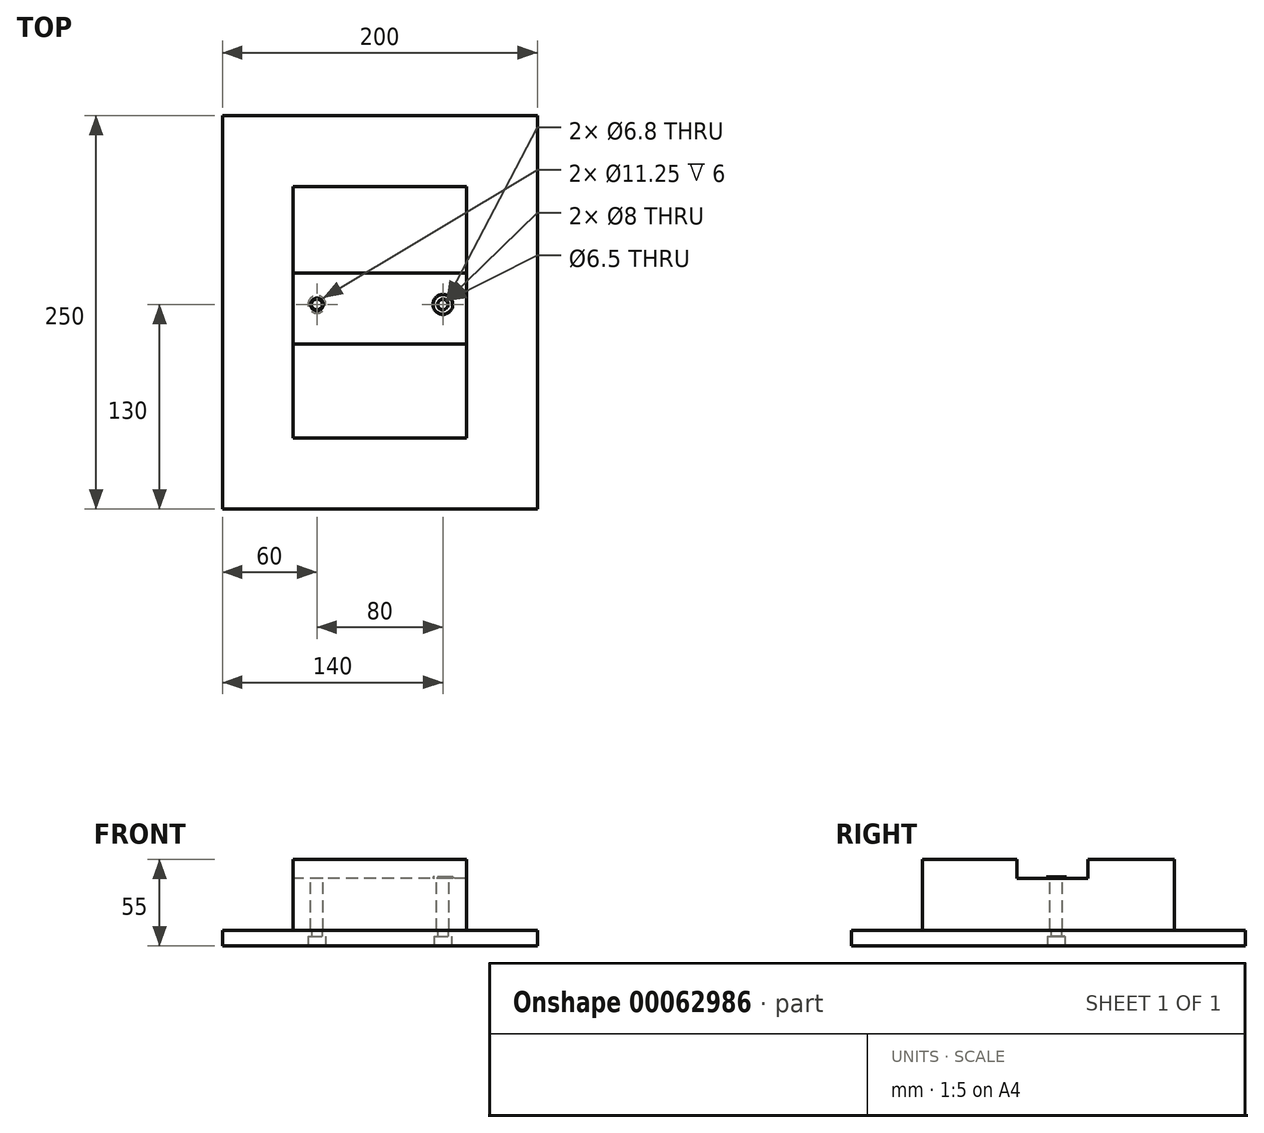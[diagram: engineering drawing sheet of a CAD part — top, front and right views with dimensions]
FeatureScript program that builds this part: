
annotation { "Feature Type Name" : "Feature", "Feature Type Description" : "" }
export const myFeature = defineFeature(function(context is Context, id is Id, definition is map)
    precondition{}
    {
        {
            var Q0;
            Q0=qCreatedBy(makeId("Right.planeOp"),FACE);
            var sketch = newSketch(context, id + "F0", { "sketchPlane" : qUnion([Q0])});
            skLineSegment(sketch, "E0.bottom", {"start": v(-80, 45) * mm, "end": v(-20, 45) * mm});
            skLineSegment(sketch, "E0.top", {"start": v(-80, 0) * mm, "end": v(80, 0) * mm});
            skLineSegment(sketch, "E0.left", {"start": v(-80, 45) * mm, "end": v(-80, 0) * mm});
            skLineSegment(sketch, "E0.right", {"start": v(80, 45) * mm, "end": v(80, 0) * mm});
            skLineSegment(sketch, "E1", {"start": v(-20, 45) * mm, "end": v(-20, 33) * mm});
            skLineSegment(sketch, "E2", {"start": v(-20, 33) * mm, "end": v(25, 33) * mm});
            skLineSegment(sketch, "E3", {"start": v(25, 33) * mm, "end": v(25, 45) * mm});
            skLineSegment(sketch, "E4.trimOffspring", {"start": v(25, 45) * mm, "end": v(80, 45) * mm});
            skSolve(sketch);
        }
        {
            var Q0;
            Q0 = qSketchRegion(id + "F0", true);
            extrude(context, id + "F1", {"entities" : qUnion([Q0]), "endBound" : BoundingType.SYMMETRIC, "depth" : 110 * mm});
        }
        {
            var Q0;
            Q0=makeQuery(id+"F1.opExtrude","SWEPT_FACE",FACE,{"disambiguationData":[OSD([sQuery(id+"F0.wireOp",EDGE,"E2")])]});
            var sketch = newSketch(context, id + "F2", { "sketchPlane" : qUnion([Q0])});
            skCircle(sketch, "E5", {"center": v(-40, 5) * mm, "radius": 4 * mm});
            skCircle(sketch, "E6", {"center": v(40, 5) * mm, "radius": 4 * mm});
            skSolve(sketch);
        }
        {
            var Q0;
            Q0 = qSketchRegion(id + "F2", true);
            extrude(context, id + "F3", {"entities" : qUnion([Q0]), "operationType" : NewBodyOperationType.REMOVE, "endBound" : BoundingType.THROUGH_ALL, "oppositeDirection" : true, "depth" : 25 * mm});
        }
        {
            var Q0;
            Q0=qCreatedBy(makeId("Top.planeOp"),FACE);
            var sketch = newSketch(context, id + "F4", { "sketchPlane" : qUnion([Q0])});
            skLineSegment(sketch, "E7.rect.bottom", {"start": v(-100, -125) * mm, "end": v(100, -125) * mm});
            skLineSegment(sketch, "E7.rect.top", {"start": v(-100, 125) * mm, "end": v(100, 125) * mm});
            skLineSegment(sketch, "E7.rect.left", {"start": v(-100, -125) * mm, "end": v(-100, 125) * mm});
            skLineSegment(sketch, "E7.rect.right", {"start": v(100, -125) * mm, "end": v(100, 125) * mm});
            skPoint(sketch, "E7.rect.middle", {"position": v(0, 0) * mm});
            skSolve(sketch);
        }
        {
            var Q0;
            Q0 = qSketchRegion(id + "F4", true);
            extrude(context, id + "F5", {"entities" : qUnion([Q0]), "oppositeDirection" : true, "depth" : 10 * mm});
        }
        {
            var Q0;
            Q0=makeQuery(id+"F5.opExtrude","CAP_FACE",FACE,{"disambiguationData":[OSD([sQuery(id+"F4.wireOp",EDGE,"E7.rect.bottom"),sQuery(id+"F4.wireOp",EDGE,"E7.rect.top"),sQuery(id+"F4.wireOp",EDGE,"E7.rect.left"),sQuery(id+"F4.wireOp",EDGE,"E7.rect.right")])],"isStart":false});
            var sketch = newSketch(context, id + "F6", { "sketchPlane" : qUnion([Q0])});
            skCircle(sketch, "E8", {"center": v(-40, -5) * mm, "radius": 3.4 * mm});
            skCircle(sketch, "E9.MirrorC", {"center": v(40, -5) * mm, "radius": 3.4 * mm});
            skSolve(sketch);
        }
        {
            var Q0;
            Q0=makeQuery(id+"F6.imprint","IMPRINT",FACE,{"disambiguationData":[TD([[makeQuery(id+"F6.imprint","IMPRINT",EDGE,{"derivedFrom":sQuery(id+"F6.wireOp",EDGE,"E8")}),-1.0]])]});
            var sketch = newSketch(context, id + "F7", { "sketchPlane" : qUnion([Q0])});
            skCircle(sketch, "E10", {"center": v(-40, -5) * mm, "radius": 5.62 * mm});
            skCircle(sketch, "E11.MirrorC", {"center": v(40, -5) * mm, "radius": 5.62 * mm});
            skSolve(sketch);
        }
        {
            var Q0;
            Q0 = qSketchRegion(id + "F6", true);
            var Q1;
            Q1=makeQuery(id+"F5.opExtrude","SWEPT_BODY",BODY,{"disambiguationData":[OSD([sQuery(id+"F4.wireOp",EDGE,"E7.rect.bottom"),sQuery(id+"F4.wireOp",EDGE,"E7.rect.top"),sQuery(id+"F4.wireOp",EDGE,"E7.rect.left"),sQuery(id+"F4.wireOp",EDGE,"E7.rect.right")])]});
            extrude(context, id + "F8", {"entities" : qUnion([Q0]), "operationType" : NewBodyOperationType.REMOVE, "endBound" : BoundingType.UP_TO_BODY, "oppositeDirection" : true, "endBoundEntityBody" : qUnion([Q1]), "depth" : 25 * mm});
        }
        {
            var Q0;
            Q0 = qSketchRegion(id + "F7", true);
            extrude(context, id + "F9", {"entities" : qUnion([Q0]), "operationType" : NewBodyOperationType.REMOVE, "oppositeDirection" : true, "depth" : 6 * mm});
        }
        {
            var Q0;
            Q0=makeQuery(id+"F1.opExtrude","SWEPT_FACE",FACE,{"disambiguationData":[OSD([sQuery(id+"F0.wireOp",EDGE,"E2")])]});
            var sketch = newSketch(context, id + "F10", { "sketchPlane" : qUnion([Q0])});
            skCircle(sketch, "E12", {"center": v(40, 5) * mm, "radius": 3.25 * mm});
            skCircle(sketch, "E13", {"center": v(40, 5) * mm, "radius": 6.33 * mm});
            skSolve(sketch);
        }
        {
            var Q0;
            Q0 = qSketchRegion(id + "F10", true);
            extrude(context, id + "F11", {"entities" : qUnion([Q0]), "depth" : 1 * mm});
        }
    });
